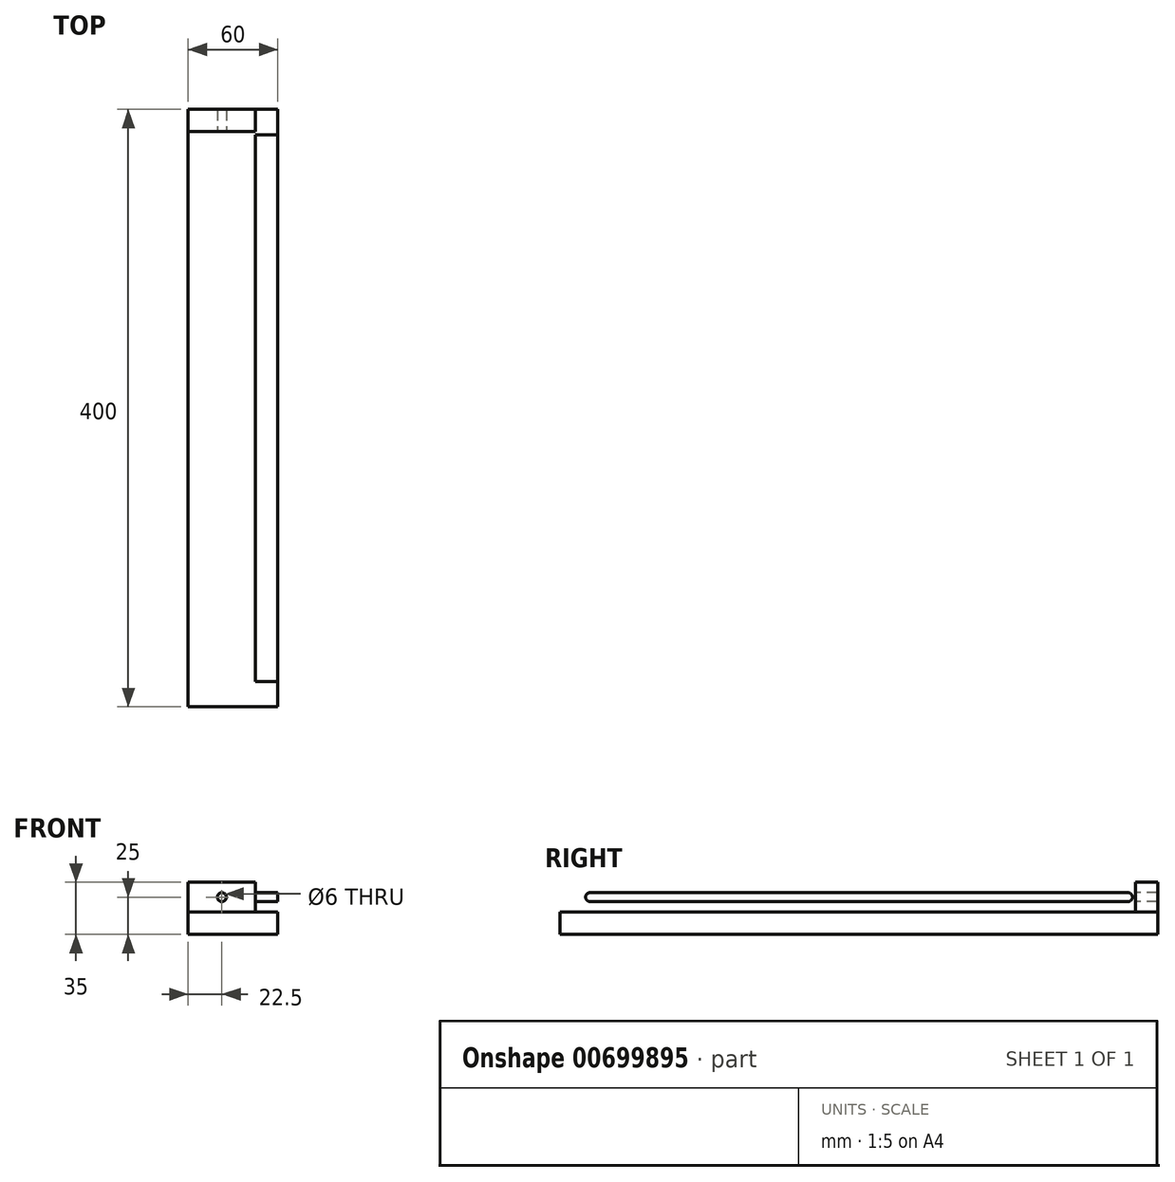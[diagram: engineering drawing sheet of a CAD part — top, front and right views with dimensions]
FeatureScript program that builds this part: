
annotation { "Feature Type Name" : "Feature", "Feature Type Description" : "" }
export const myFeature = defineFeature(function(context is Context, id is Id, definition is map)
    precondition{}
    {
        {
            var Q0;
            Q0=qCreatedBy(makeId("Front.planeOp"),FACE);
            var sketch = newSketch(context, id + "F0", { "sketchPlane" : qUnion([Q0])});
            skLineSegment(sketch, "E0.bottom", {"start": v(30, 7.5) * mm, "end": v(-30, 7.5) * mm});
            skLineSegment(sketch, "E0.top", {"start": v(30, -7.5) * mm, "end": v(-30, -7.5) * mm});
            skLineSegment(sketch, "E0.left", {"start": v(30, 7.5) * mm, "end": v(30, -7.5) * mm});
            skLineSegment(sketch, "E0.right", {"start": v(-30, 7.5) * mm, "end": v(-30, -7.5) * mm});
            skPoint(sketch, "E0.middle", {"position": v(0, 0) * mm});
            skSolve(sketch);
        }
        {
            var Q0;
            Q0 = qSketchRegion(id + "F0", true);
            extrude(context, id + "F1", {"entities" : qUnion([Q0]), "endBound" : BoundingType.SYMMETRIC, "depth" : 400 * mm, "offsetDistance" : 25 * mm});
        }
        {
            var Q0;
            Q0=makeQuery(id+"F1.opExtrude","CAP_FACE",FACE,{"disambiguationData":[OSD([sQuery(id+"F0.wireOp",EDGE,"E0.bottom"),sQuery(id+"F0.wireOp",EDGE,"E0.top"),sQuery(id+"F0.wireOp",EDGE,"E0.left"),sQuery(id+"F0.wireOp",EDGE,"E0.right")])],"isStart":false});
            var sketch = newSketch(context, id + "F2", { "sketchPlane" : qUnion([Q0])});
            skLineSegment(sketch, "E1.bottom", {"start": v(30, 7.5) * mm, "end": v(15, 7.5) * mm});
            skLineSegment(sketch, "E1.top", {"start": v(30, 27.5) * mm, "end": v(15, 27.5) * mm});
            skLineSegment(sketch, "E1.left", {"start": v(30, 7.5) * mm, "end": v(30, 27.5) * mm});
            skLineSegment(sketch, "E1.right", {"start": v(15, 7.5) * mm, "end": v(15, 27.5) * mm});
            skSolve(sketch);
        }
        {
            var Q0;
            Q0 = qSketchRegion(id + "F2", true);
            var Q1;
            Q1=makeQuery(id+"F1.opExtrude","CAP_FACE",FACE,{"disambiguationData":[OSD([sQuery(id+"F0.wireOp",EDGE,"E0.bottom"),sQuery(id+"F0.wireOp",EDGE,"E0.top"),sQuery(id+"F0.wireOp",EDGE,"E0.left"),sQuery(id+"F0.wireOp",EDGE,"E0.right")])],"isStart":true});
            extrude(context, id + "F3", {"entities" : qUnion([Q0]), "operationType" : NewBodyOperationType.ADD, "endBound" : BoundingType.UP_TO_SURFACE, "oppositeDirection" : true, "depth" : 25 * mm, "endBoundEntityFace" : qUnion([Q1]), "offsetDistance" : 25 * mm});
        }
        {
            var Q0;
            Q0=makeQuery(id+"F3.opExtrude","SWEPT_FACE",FACE,{"disambiguationData":[OSD([sQuery(id+"F2.wireOp",EDGE,"E1.right")])]});
            var sketch = newSketch(context, id + "F4", { "sketchPlane" : qUnion([Q0])});
            skLineSegment(sketch, "E2", {"start": v(180, 17.5) * mm, "end": v(-180, 17.5) * mm});
            skPoint(sketch, "E2.startSnap0", {"position": v(200, 17.5) * mm});
            skArc(sketch, "E3.0.startCap", {"start": v(180, 20.5) * mm, "mid": v(183, 17.5) * mm, "end": v(180, 14.5) * mm});
            skArc(sketch, "E3.0.endCap", {"start": v(-180, 14.5) * mm, "mid": v(-183, 17.5) * mm, "end": v(-180, 20.5) * mm});
            skLineSegment(sketch, "E3.0.left", {"start": v(180, 14.5) * mm, "end": v(-180, 14.5) * mm});
            skLineSegment(sketch, "E3.0.right", {"start": v(180, 20.5) * mm, "end": v(-180, 20.5) * mm});
            skSolve(sketch);
        }
        {
            var Q0;
            Q0=makeQuery(id+"F4.imprint","IMPRINT",FACE,{"disambiguationData":[TD([[makeQuery(id+"F4.imprint","IMPRINT",EDGE,{"derivedFrom":sQuery(id+"F4.wireOp",EDGE,"E3.0.startCap")}),-1.0]])]});
            extrude(context, id + "F5", {"entities" : qUnion([Q0]), "operationType" : NewBodyOperationType.REMOVE, "endBound" : BoundingType.THROUGH_ALL, "oppositeDirection" : true, "depth" : 25 * mm, "offsetDistance" : 25 * mm});
        }
        {
            var Q0;
            Q0=makeQuery(id+"F1.opExtrude","SWEPT_FACE",FACE,{"disambiguationData":[OSD([sQuery(id+"F0.wireOp",EDGE,"E0.bottom")])]});
            var sketch = newSketch(context, id + "F6", { "sketchPlane" : qUnion([Q0])});
            skLineSegment(sketch, "E4.bottom", {"start": v(-30, 200) * mm, "end": v(15, 200) * mm});
            skLineSegment(sketch, "E4.top", {"start": v(-30, 185) * mm, "end": v(15, 185) * mm});
            skLineSegment(sketch, "E4.left", {"start": v(-30, 200) * mm, "end": v(-30, 185) * mm});
            skLineSegment(sketch, "E4.right", {"start": v(15, 200) * mm, "end": v(15, 185) * mm});
            skSolve(sketch);
        }
        {
            var Q0;
            Q0 = qSketchRegion(id + "F6", true);
            extrude(context, id + "F7", {"entities" : qUnion([Q0]), "operationType" : NewBodyOperationType.ADD, "depth" : 20 * mm, "offsetDistance" : 25 * mm});
        }
        {
            var Q0;
            Q0=makeQuery(id+"F7.opExtrude","SWEPT_FACE",FACE,{"disambiguationData":[OSD([sQuery(id+"F6.wireOp",EDGE,"E4.top")])]});
            var sketch = newSketch(context, id + "F8", { "sketchPlane" : qUnion([Q0])});
            skLineSegment(sketch, "E5", {"start": v(15, 7.5) * mm, "end": v(-30, 27.5) * mm, "construction": true});
            skCircle(sketch, "E6", {"center": v(-7.5, 17.5) * mm, "radius": 3 * mm});
            skSolve(sketch);
        }
        {
            var Q0;
            Q0 = qSketchRegion(id + "F8", true);
            extrude(context, id + "F9", {"entities" : qUnion([Q0]), "operationType" : NewBodyOperationType.REMOVE, "endBound" : BoundingType.THROUGH_ALL, "oppositeDirection" : true, "depth" : 25 * mm, "offsetDistance" : 25 * mm});
        }
    });
